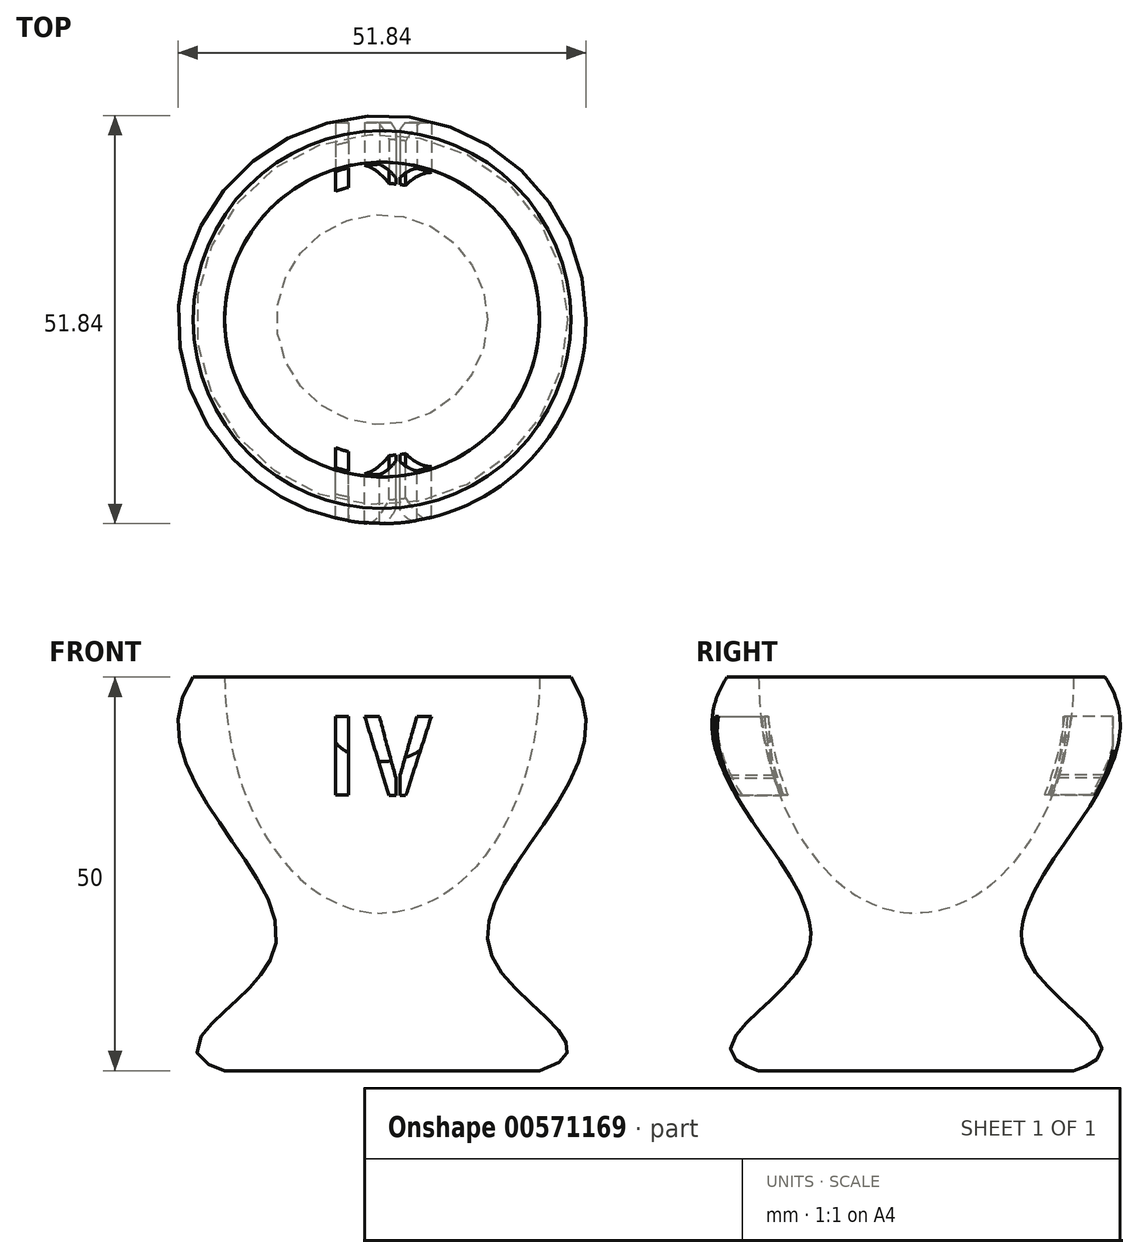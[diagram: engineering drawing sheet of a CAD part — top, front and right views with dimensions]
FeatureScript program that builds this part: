
annotation { "Feature Type Name" : "Feature", "Feature Type Description" : "" }
export const myFeature = defineFeature(function(context is Context, id is Id, definition is map)
    precondition{}
    {
        {
            var Q0;
            Q0=qCreatedBy(makeId("Front.planeOp"),FACE);
            var sketch = newSketch(context, id + "F0", { "sketchPlane" : qUnion([Q0])});
            skEllipse(sketch, "E0", {"center": v(0, 0) * mm, "majorRadius": 30 * mm, "minorRadius": 20 * mm, "majorAxis": v(0, 1)});
            skLineSegment(sketch, "E1", {"start": v(0, 67.87) * mm, "end": v(0, -50) * mm, "construction": true});
            skPoint(sketch, "E1.endSnap0", {"position": v(0, -30) * mm});
            skLineSegment(sketch, "E2", {"start": v(-20, 0) * mm, "end": v(-24, 0) * mm});
            skLineSegment(sketch, "E3", {"start": v(0, -50) * mm, "end": v(-20, -50) * mm});
            skFitSpline(sketch, "E4", {"points": [v(-24, 0) * mm, v(-13.76, -35.01) * mm, v(-20, -50) * mm], "startDerivative": vector(-42.18, -62.06) * mm, "endDerivative": vector(74.8, -22.1) * mm});
            skLineSegment(sketch, "E5", {"start": v(0, -50) * mm, "end": v(0, -30) * mm});
            skSolve(sketch);
        }
        {
            var Q0;
            {var subQ0=sQuery(id+"F0.wireOp",EDGE,"E2");Q0=makeQuery(id+"F0.imprint","IMPRINT",FACE,{"disambiguationData":[TD([[makeQuery(id+"F0.imprint","IMPRINT",EDGE,{"derivedFrom":subQ0}),1.0]])]});}
            var Q1;
            Q1=sQuery(id+"F0.wireOp",EDGE,"E1");
            revolve(context, id + "F1", {"entities" : qUnion([Q0]), "axis" : qUnion([Q1]), "revolveType" : RevolveType.FULL});
        }
        {
            var Q0;
            Q0=qCreatedBy(makeId("Front.planeOp"),FACE);
            var sketch = newSketch(context, id + "F2", { "sketchPlane" : qUnion([Q0])});
            skText(sketch, "E6", { "text": "IV", "fontName": "AllertaStencil-Regular.ttf"});
            const initialGuessF2  = {"E6": [-0.0072, -0.015, 1, 0, 0.01]};
            skSetInitialGuess(sketch, initialGuessF2);
            skSolve(sketch);
        }
        {
            var Q0;
            Q0 = qSketchRegion(id + "F2", true);
            extrude(context, id + "F3", {"entities" : qUnion([Q0]), "operationType" : NewBodyOperationType.REMOVE, "depth" : 57.6 * mm, "offsetDistance" : 25 * mm});
        }
        {
            var Q0;
            Q0 = qSketchRegion(id + "F2", true);
            extrude(context, id + "F4", {"entities" : qUnion([Q0]), "operationType" : NewBodyOperationType.REMOVE, "oppositeDirection" : true, "depth" : 25 * mm, "offsetDistance" : 25 * mm});
        }
    });
